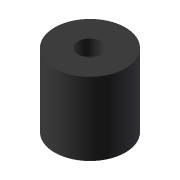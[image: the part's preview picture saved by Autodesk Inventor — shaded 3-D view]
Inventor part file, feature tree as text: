
AUTODESK INVENTOR PART (.ipt)
format: ipt  version: 2019.4 (Build 234330000, 330)  size: 110,592 bytes
history: native  units: mm
features: sketch x4, extrude x3, projected_geometry x2
ambient origin geometry x8: Origin, YZ Plane, XZ Plane, XY Plane, X Axis, Y Axis, Z Axis, Center Point
bodies: Solid1 (feature_tree)
feature tree (9):
  extrude  "Extrusion1"  Depth=9.0mm
  extrude  "Extrusion2"  Depth=3.3mm TaperAngle=0.0deg
  sketch  "Sketch3"  dims[d5=3.0mm d6=2.0mm d7=0.0mm]
  extrude  "Extrusion3"  Depth=2.0mm TaperAngle=0.0deg
  sketch  "Sketch1"  dims[d0=3.0mm d1=9.0mm]
  sketch  "Sketch2"  dims[d2=5.55mm d3=3.3mm d4=0.0mm]
  projected_geometry  "Projected Loop1"
  sketch  "Sketch4"  dims[d8=6.1mm d9=4.0mm d10=0.0mm]
  projected_geometry  "Projected Loop2"
